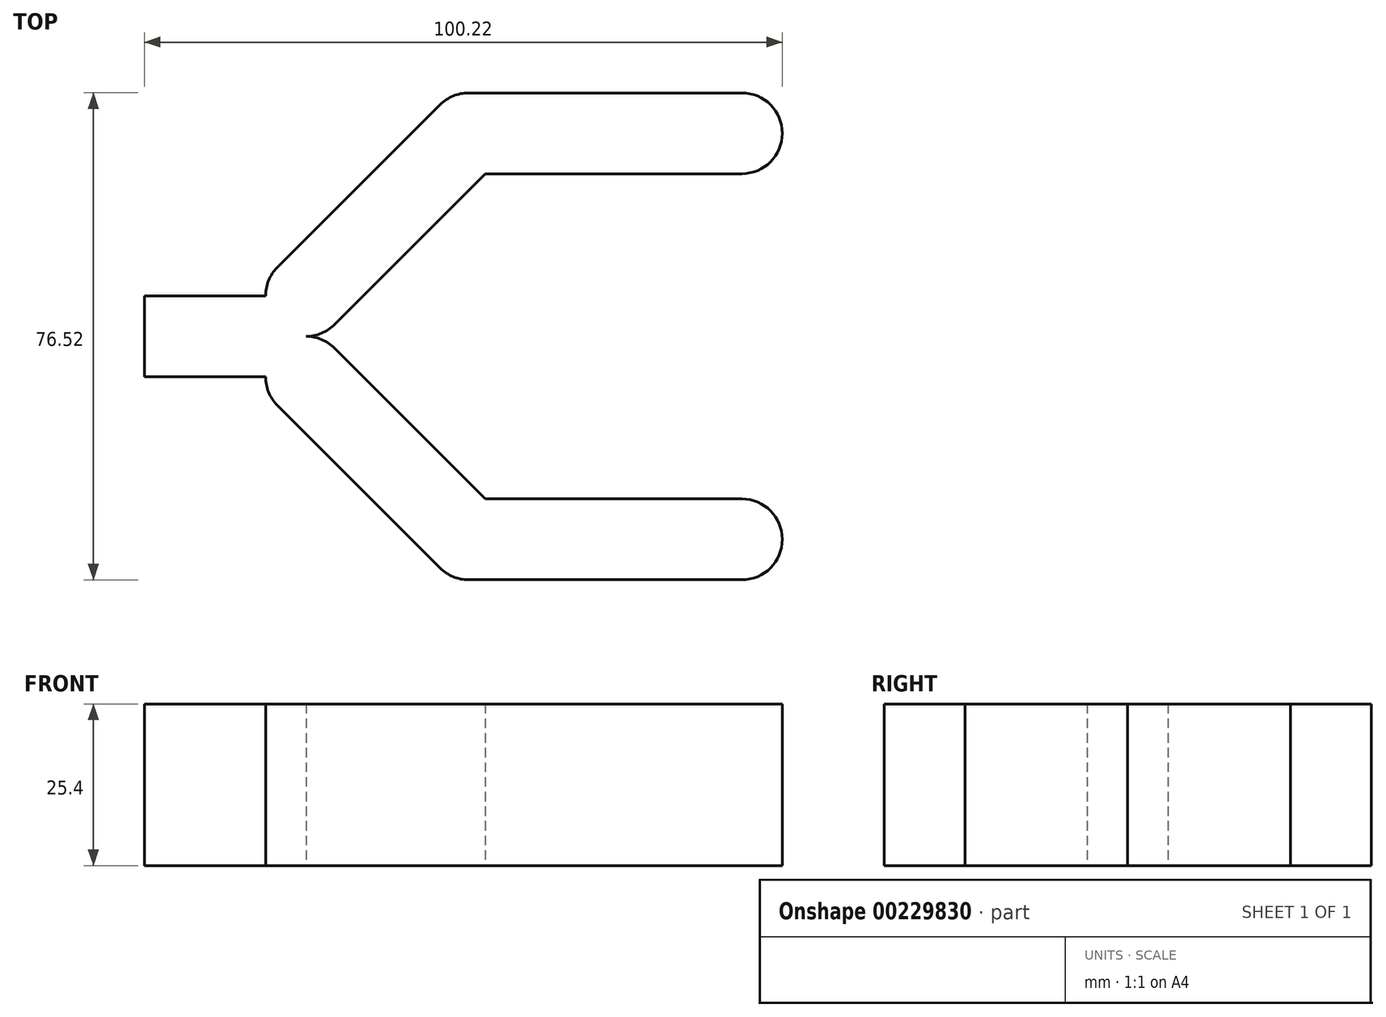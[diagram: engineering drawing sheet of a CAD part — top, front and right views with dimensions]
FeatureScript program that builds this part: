
annotation { "Feature Type Name" : "Feature", "Feature Type Description" : "" }
export const myFeature = defineFeature(function(context is Context, id is Id, definition is map)
    precondition{}
    {
        {
            var Q0;
            Q0=qCreatedBy(makeId("Top.planeOp"),FACE);
            var sketch = newSketch(context, id + "F0", { "sketchPlane" : qUnion([Q0])});
            skLineSegment(sketch, "E0.bottom", {"start": v(12.7, 6.35) * mm, "end": v(-12.7, 6.35) * mm});
            skLineSegment(sketch, "E0.top", {"start": v(12.7, -6.35) * mm, "end": v(-12.7, -6.35) * mm});
            skLineSegment(sketch, "E0.left", {"start": v(12.7, 6.35) * mm, "end": v(12.7, -6.35) * mm});
            skLineSegment(sketch, "E0.right", {"start": v(-12.7, 6.35) * mm, "end": v(-12.7, -6.35) * mm});
            skPoint(sketch, "E0.middle", {"position": v(0, 0) * mm});
            skLineSegment(sketch, "E1", {"start": v(12.7, 6.35) * mm, "end": v(38.26, 31.9) * mm});
            skLineSegment(sketch, "E2", {"start": v(38.26, 31.9) * mm, "end": v(81.17, 31.9) * mm});
            skLineSegment(sketch, "E3.MirrorCS", {"start": v(12.7, -6.35) * mm, "end": v(38.26, -31.9) * mm});
            skLineSegment(sketch, "E4.MirrorCS", {"start": v(38.26, -31.9) * mm, "end": v(81.17, -31.9) * mm});
            skArc(sketch, "E5.0.startCap", {"start": v(17.2, 1.86) * mm, "mid": v(8.2, 1.86) * mm, "end": v(8.2, 10.84) * mm});
            skArc(sketch, "E5.0.endCap", {"start": v(33.77, 36.4) * mm, "mid": v(42.75, 36.4) * mm, "end": v(42.75, 27.42) * mm});
            skLineSegment(sketch, "E5.0.left", {"start": v(8.2, 10.84) * mm, "end": v(33.77, 36.4) * mm});
            skLineSegment(sketch, "E5.0.right", {"start": v(17.2, 1.86) * mm, "end": v(42.75, 27.42) * mm});
            skArc(sketch, "E5.1.startCap", {"start": v(38.26, 25.56) * mm, "mid": v(31.9, 31.9) * mm, "end": v(38.26, 38.26) * mm});
            skArc(sketch, "E5.1.endCap", {"start": v(81.17, 38.26) * mm, "mid": v(87.52, 31.9) * mm, "end": v(81.17, 25.56) * mm});
            skLineSegment(sketch, "E5.1.left", {"start": v(38.26, 38.26) * mm, "end": v(81.17, 38.26) * mm});
            skLineSegment(sketch, "E5.1.right", {"start": v(38.26, 25.56) * mm, "end": v(81.17, 25.56) * mm});
            skArc(sketch, "E5.2.startCap", {"start": v(8.2, -10.84) * mm, "mid": v(8.2, -1.86) * mm, "end": v(17.2, -1.86) * mm});
            skArc(sketch, "E5.2.endCap", {"start": v(42.75, -27.42) * mm, "mid": v(42.75, -36.4) * mm, "end": v(33.77, -36.4) * mm});
            skLineSegment(sketch, "E5.2.left", {"start": v(17.2, -1.86) * mm, "end": v(42.75, -27.42) * mm});
            skLineSegment(sketch, "E5.2.right", {"start": v(8.2, -10.84) * mm, "end": v(33.77, -36.4) * mm});
            skArc(sketch, "E5.3.startCap", {"start": v(38.26, -38.26) * mm, "mid": v(31.9, -31.9) * mm, "end": v(38.26, -25.56) * mm});
            skArc(sketch, "E5.3.endCap", {"start": v(81.17, -25.56) * mm, "mid": v(87.52, -31.9) * mm, "end": v(81.17, -38.26) * mm});
            skLineSegment(sketch, "E5.3.left", {"start": v(38.26, -25.56) * mm, "end": v(81.17, -25.56) * mm});
            skLineSegment(sketch, "E5.3.right", {"start": v(38.26, -38.26) * mm, "end": v(81.17, -38.26) * mm});
            skSolve(sketch);
        }
        {
            var Q0;
            Q0 = qSketchRegion(id + "F0", true);
            extrude(context, id + "F1", {"entities" : qUnion([Q0]), "depth" : 25.4 * mm});
        }
    });
